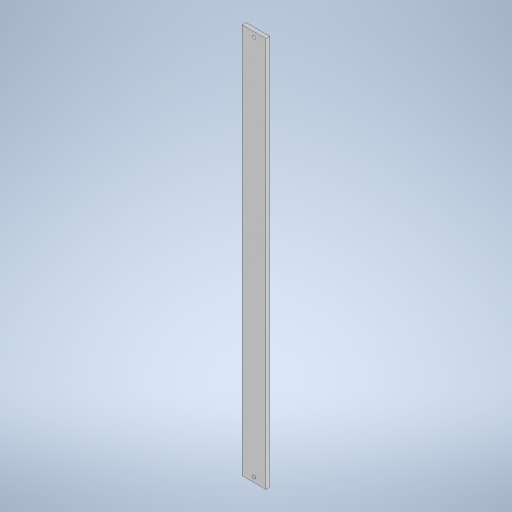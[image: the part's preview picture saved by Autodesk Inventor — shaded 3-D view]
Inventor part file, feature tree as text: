
AUTODESK INVENTOR PART (.ipt)
format: ipt  version: 2023.2 (Build 272271030, 271C)  size: 260,608 bytes
history: native  units: mm
features: sketch x2, other x1, extrude x1, hole x1
ambient origin geometry x8: Origin, YZ Plane, XZ Plane, XY Plane, X Axis, Y Axis, Z Axis, Center Point
bodies: Body1 (feature_tree)
feature tree (5):
  other  "Sólido1"
  extrude  "Extrusão1"  Depth=5.0mm
  hole  "Furo3"  [1 undecoded]
  sketch  "Esboço1"  dims[d0=30.0mm d1=5.0mm]
  sketch  "Esboço4"  dims[d2=494.0mm d3=0.0mm d30=30.0mm d31=15.0mm d32=15.0mm d33=6.25mm d34=6.25mm d35=4.0mm d36=17.0mm d37=3.023mm d38=2.0mm d39=14.3117mm d40=0.5mm d41=20.594885mm]
note: 1 required parameter value undecoded (feature->parameter linkage not recoverable at this tier; creation-order binding heuristic only, values carry confidence <= 0.55)
